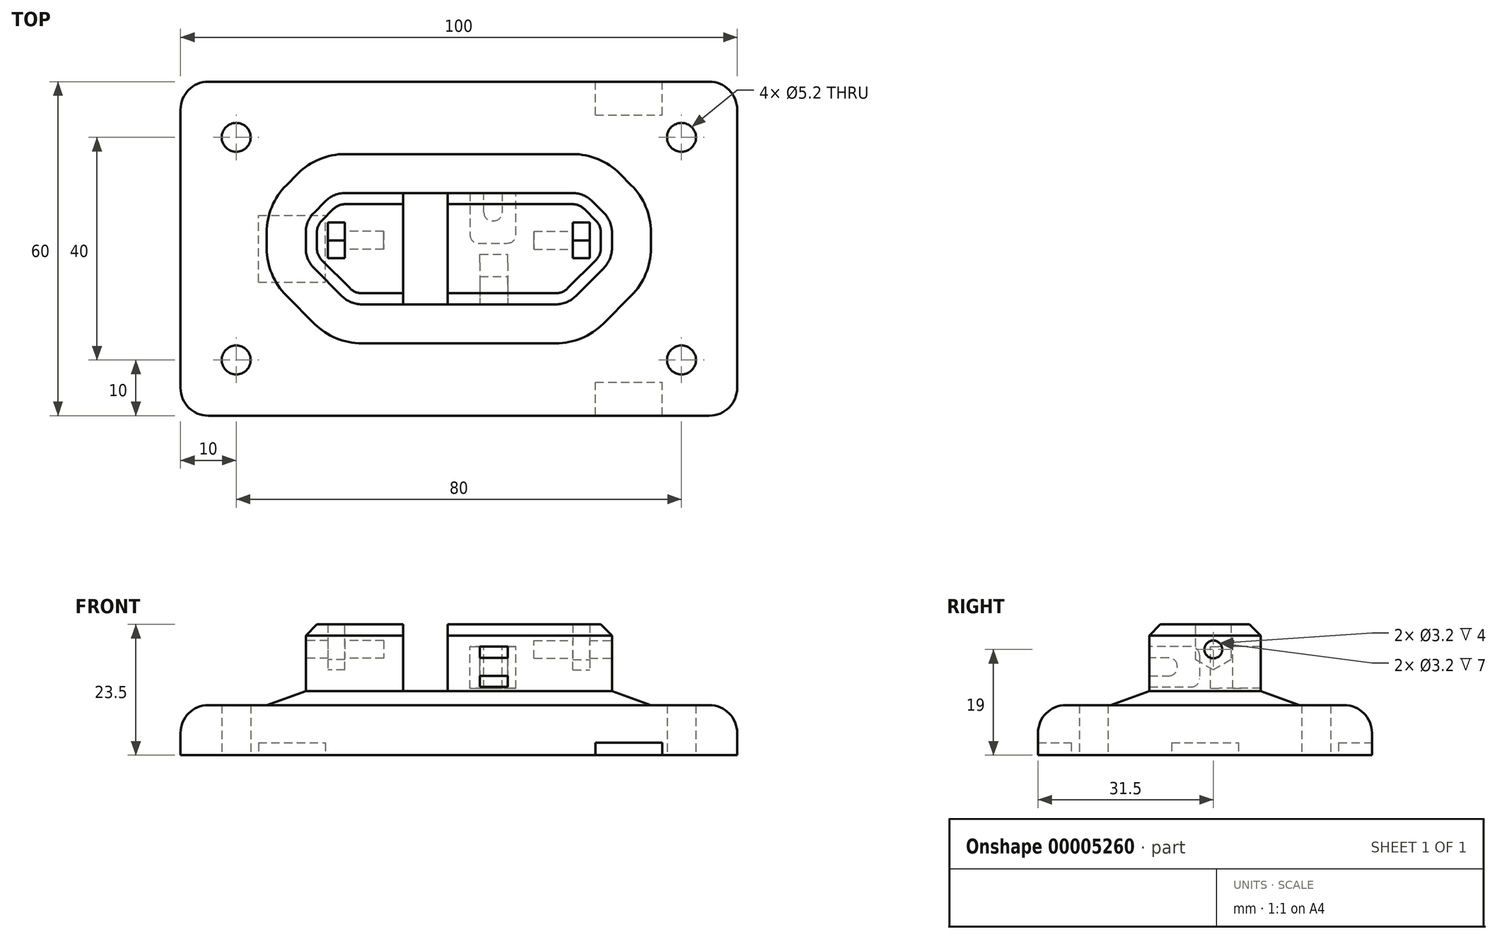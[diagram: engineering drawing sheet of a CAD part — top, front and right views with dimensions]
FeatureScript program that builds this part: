
annotation { "Feature Type Name" : "Feature", "Feature Type Description" : "" }
export const myFeature = defineFeature(function(context is Context, id is Id, definition is map)
    precondition{}
    {
        {
            var Q0;
            Q0=qCreatedBy(makeId("Top.planeOp"),FACE);
            var sketch = newSketch(context, id + "F0", { "sketchPlane" : qUnion([Q0])});
            skLineSegment(sketch, "E0.rect.bottom", {"start": v(-45, 30) * mm, "end": v(45, 30) * mm});
            skLineSegment(sketch, "E0.rect.top", {"start": v(-45, -30) * mm, "end": v(45, -30) * mm});
            skLineSegment(sketch, "E0.rect.left", {"start": v(-50, 25) * mm, "end": v(-50, -25) * mm});
            skLineSegment(sketch, "E0.rect.right", {"start": v(50, 25) * mm, "end": v(50, -25) * mm});
            skPoint(sketch, "E0.rect.middle", {"position": v(0, 0) * mm});
            skCircle(sketch, "E1", {"center": v(-40, 20) * mm, "radius": 2.6 * mm});
            skCircle(sketch, "E2", {"center": v(40, 20) * mm, "radius": 2.6 * mm});
            skCircle(sketch, "E3", {"center": v(40, -20) * mm, "radius": 2.6 * mm});
            skCircle(sketch, "E4", {"center": v(-40, -20) * mm, "radius": 2.6 * mm});
            skPoint(sketch, "E5.visualSharp", {"position": v(-50, 30) * mm});
            skArc(sketch, "E5.filletArc", {"start": v(-45, 30) * mm, "mid": v(-48.54, 28.54) * mm, "end": v(-50, 25) * mm});
            skPoint(sketch, "E6.visualSharp", {"position": v(50, 30) * mm});
            skArc(sketch, "E6.filletArc", {"start": v(50, 25) * mm, "mid": v(48.54, 28.54) * mm, "end": v(45, 30) * mm});
            skPoint(sketch, "E7.visualSharp", {"position": v(50, -30) * mm});
            skArc(sketch, "E7.filletArc", {"start": v(45, -30) * mm, "mid": v(48.54, -28.54) * mm, "end": v(50, -25) * mm});
            skPoint(sketch, "E8.visualSharp", {"position": v(-50, -30) * mm});
            skArc(sketch, "E8.filletArc", {"start": v(-50, -25) * mm, "mid": v(-48.54, -28.54) * mm, "end": v(-45, -30) * mm});
            skSolve(sketch);
        }
        {
            var Q0;
            Q0=qSketchRegion(id+"F0",true);
            extrude(context, id + "F1", {"entities" : qUnion([Q0]), "depth" : 9 * mm});
        }
        {
            var Q0;
            Q0=makeQuery(id+"F1.opExtrude","CAP_FACE",FACE,{"disambiguationData":[OSD([sQuery(id+"F0.wireOp",EDGE,"E0.rect.bottom"),sQuery(id+"F0.wireOp",EDGE,"E0.rect.top"),sQuery(id+"F0.wireOp",EDGE,"E0.rect.left"),sQuery(id+"F0.wireOp",EDGE,"E0.rect.right"),sQuery(id+"F0.wireOp",EDGE,"E1"),sQuery(id+"F0.wireOp",EDGE,"E2"),sQuery(id+"F0.wireOp",EDGE,"E3"),sQuery(id+"F0.wireOp",EDGE,"E4"),sQuery(id+"F0.wireOp",EDGE,"E5.filletArc"),sQuery(id+"F0.wireOp",EDGE,"E6.filletArc"),sQuery(id+"F0.wireOp",EDGE,"E7.filletArc"),sQuery(id+"F0.wireOp",EDGE,"E8.filletArc")])],"isStart":true});
            var sketch = newSketch(context, id + "F2", { "sketchPlane" : qUnion([Q0])});
            skLineSegment(sketch, "E9.rect.bottom", {"start": v(-36, 6) * mm, "end": v(-24, 6) * mm});
            skLineSegment(sketch, "E9.rect.top", {"start": v(-36, -6) * mm, "end": v(-24, -6) * mm});
            skLineSegment(sketch, "E9.rect.left", {"start": v(-36, 6) * mm, "end": v(-36, -6) * mm});
            skLineSegment(sketch, "E9.rect.right", {"start": v(-24, 6) * mm, "end": v(-24, -6) * mm});
            skPoint(sketch, "E9.rect.middle", {"position": v(-30, 0) * mm});
            skLineSegment(sketch, "E10.rect.bottom", {"start": v(24.52, 36) * mm, "end": v(36.52, 36) * mm});
            skLineSegment(sketch, "E10.rect.top", {"start": v(24.52, 24) * mm, "end": v(36.52, 24) * mm});
            skLineSegment(sketch, "E10.rect.left", {"start": v(24.52, 36) * mm, "end": v(24.52, 24) * mm});
            skLineSegment(sketch, "E10.rect.right", {"start": v(36.52, 36) * mm, "end": v(36.52, 24) * mm});
            skPoint(sketch, "E10.rect.middle", {"position": v(30.52, 30) * mm});
            skLineSegment(sketch, "E11.rect.bottom", {"start": v(24.52, -24) * mm, "end": v(36.52, -24) * mm});
            skLineSegment(sketch, "E11.rect.top", {"start": v(24.52, -36) * mm, "end": v(36.52, -36) * mm});
            skLineSegment(sketch, "E11.rect.left", {"start": v(24.52, -24) * mm, "end": v(24.52, -36) * mm});
            skLineSegment(sketch, "E11.rect.right", {"start": v(36.52, -24) * mm, "end": v(36.52, -36) * mm});
            skPoint(sketch, "E11.rect.middle", {"position": v(30.52, -30) * mm});
            skLineSegment(sketch, "E12", {"start": v(0, 0) * mm, "end": v(50, 0) * mm});
            skSolve(sketch);
        }
        {
            var Q0;
            Q0=qSketchRegion(id+"F2",true);
            extrude(context, id + "F3", {"entities" : qUnion([Q0]), "operationType" : NewBodyOperationType.REMOVE, "oppositeDirection" : true, "depth" : 2.25 * mm});
        }
        {
            var Q0;
            Q0=makeQuery(id+"F1.opExtrude","CAP_FACE",FACE,{"disambiguationData":[OSD([sQuery(id+"F0.wireOp",EDGE,"E0.rect.bottom"),sQuery(id+"F0.wireOp",EDGE,"E0.rect.top"),sQuery(id+"F0.wireOp",EDGE,"E0.rect.left"),sQuery(id+"F0.wireOp",EDGE,"E0.rect.right"),sQuery(id+"F0.wireOp",EDGE,"E1"),sQuery(id+"F0.wireOp",EDGE,"E2"),sQuery(id+"F0.wireOp",EDGE,"E3"),sQuery(id+"F0.wireOp",EDGE,"E4"),sQuery(id+"F0.wireOp",EDGE,"E5.filletArc"),sQuery(id+"F0.wireOp",EDGE,"E6.filletArc"),sQuery(id+"F0.wireOp",EDGE,"E7.filletArc"),sQuery(id+"F0.wireOp",EDGE,"E8.filletArc")])],"isStart":false});
            var sketch = newSketch(context, id + "F4", { "sketchPlane" : qUnion([Q0])});
            skPoint(sketch, "E13.orphan", {"position": v(-50, 0) * mm});
            skPoint(sketch, "E14.end.orphan", {"position": v(50, 0) * mm});
            skLineSegment(sketch, "E15.rect.bottom", {"start": v(-27.5, 10) * mm, "end": v(27.5, 10) * mm});
            skLineSegment(sketch, "E15.rect.top", {"start": v(-27.5, -10) * mm, "end": v(27.5, -10) * mm});
            skLineSegment(sketch, "E15.rect.left", {"start": v(-27.5, 10) * mm, "end": v(-27.5, -10) * mm});
            skLineSegment(sketch, "E15.rect.right", {"start": v(27.5, 10) * mm, "end": v(27.5, -10) * mm});
            skPoint(sketch, "E15.rect.middle", {"position": v(0, 0) * mm});
            skSolve(sketch);
        }
        {
            var Q0;
            Q0=qSketchRegion(id+"F4",true);
            extrude(context, id + "F5", {"entities" : qUnion([Q0]), "operationType" : NewBodyOperationType.ADD, "depth" : 14.5 * mm});
        }
        {
            var Q0;
            Q0=makeQuery(id+"F5.opExtrude","SWEPT_EDGE",EDGE,{"disambiguationData":[OSD([sQuery(id+"F4.wireOp",EDGE,"E15.rect.top"),sQuery(id+"F4.wireOp",EDGE,"E15.rect.left")])]});
            var Q1;
            Q1=makeQuery(id+"F5.opExtrude","SWEPT_EDGE",EDGE,{"disambiguationData":[OSD([sQuery(id+"F4.wireOp",EDGE,"E15.rect.top"),sQuery(id+"F4.wireOp",EDGE,"E15.rect.right")])]});
            chamfer(context, id + "F6", {"entities" : qUnion([Q0, Q1]), "width" : 8 * mm, "tangentPropagation" : true});
        }
        {
            var Q0;
            Q0=makeQuery(id+"F5.opExtrude","SWEPT_EDGE",EDGE,{"disambiguationData":[OSD([sQuery(id+"F4.wireOp",EDGE,"E15.rect.bottom"),sQuery(id+"F4.wireOp",EDGE,"E15.rect.left")])]});
            var Q1;
            Q1=makeQuery(id+"F5.opExtrude","SWEPT_EDGE",EDGE,{"disambiguationData":[OSD([sQuery(id+"F4.wireOp",EDGE,"E15.rect.bottom"),sQuery(id+"F4.wireOp",EDGE,"E15.rect.right")])]});
            chamfer(context, id + "F7", {"entities" : qUnion([Q0, Q1]), "width" : 5 * mm, "tangentPropagation" : true});
        }
        {
            var Q0;
            Q0=makeQuery(id+"F5.opExtrude","CAP_FACE",FACE,{"disambiguationData":[OSD([sQuery(id+"F4.wireOp",EDGE,"E15.rect.bottom"),sQuery(id+"F4.wireOp",EDGE,"E15.rect.top"),sQuery(id+"F4.wireOp",EDGE,"E15.rect.left"),sQuery(id+"F4.wireOp",EDGE,"E15.rect.right")])],"isStart":false});
            var sketch = newSketch(context, id + "F8", { "sketchPlane" : qUnion([Q0])});
            skLineSegment(sketch, "E16.rect.bottom", {"start": v(-10, 10) * mm, "end": v(-2, 10) * mm});
            skLineSegment(sketch, "E16.rect.top", {"start": v(-10, -10) * mm, "end": v(-2, -10) * mm});
            skLineSegment(sketch, "E16.rect.left", {"start": v(-10, 10) * mm, "end": v(-10, -10) * mm});
            skLineSegment(sketch, "E16.rect.right", {"start": v(-2, 10) * mm, "end": v(-2, -10) * mm});
            skPoint(sketch, "E16.rect.middle", {"position": v(-6, 0) * mm});
            skSolve(sketch);
        }
        {
            var Q0;
            Q0=qSketchRegion(id+"F8",true);
            extrude(context, id + "F9", {"entities" : qUnion([Q0]), "operationType" : NewBodyOperationType.REMOVE, "oppositeDirection" : true, "depth" : 12 * mm});
        }
        {
            var Q0;
            {var subQ0=sQuery(id+"F4.wireOp",EDGE,"E15.rect.bottom");var subQ1=sQuery(id+"F4.wireOp",EDGE,"E15.rect.top");var subQ2=sQuery(id+"F4.wireOp",EDGE,"E15.rect.right");Q0=makeQuery(id+"F9.boolean.opBoolean","SPLIT",FACE,{"disambiguationData":[TD([makeQuery(id+"F5.opExtrude","SWEPT_FACE",FACE,{"disambiguationData":[OSD([subQ2])]})])],"derivedFrom":makeQuery(id+"F5.opExtrude","CAP_FACE",FACE,{"disambiguationData":[OSD([subQ0,subQ1,sQuery(id+"F4.wireOp",EDGE,"E15.rect.left"),subQ2])],"isStart":false})});}
            cPlane(context, id + "F10", {"entities" : qUnion([Q0]), "cplaneType" : CPlaneType.OFFSET, "offset" : 4 * mm, "oppositeDirection" : true, "width" : 150 * mm, "height" : 150 * mm});
        }
        {
            var Q0;
            Q0=makeQuery(id+"F5.opExtrude","SWEPT_FACE",FACE,{"disambiguationData":[OSD([sQuery(id+"F4.wireOp",EDGE,"E15.rect.left")])]});
            var sketch = newSketch(context, id + "F11", { "sketchPlane" : qUnion([Q0])});
            skCircle(sketch, "E17", {"center": v(-1.5, 19) * mm, "radius": 1.6 * mm});
            skSolve(sketch);
        }
        {
            var Q0;
            Q0=qSketchRegion(id+"F11",true);
            extrude(context, id + "F12", {"entities" : qUnion([Q0]), "operationType" : NewBodyOperationType.REMOVE, "oppositeDirection" : true, "depth" : 14 * mm});
        }
        {
            var Q0;
            Q0=makeQuery(id+"F5.opExtrude","SWEPT_FACE",FACE,{"disambiguationData":[OSD([sQuery(id+"F4.wireOp",EDGE,"E15.rect.right")])]});
            var sketch = newSketch(context, id + "F13", { "sketchPlane" : qUnion([Q0])});
            skCircle(sketch, "E18", {"center": v(1.5, 19) * mm, "radius": 1.6 * mm});
            skSolve(sketch);
        }
        {
            var Q0;
            Q0=qSketchRegion(id+"F13",true);
            extrude(context, id + "F14", {"entities" : qUnion([Q0]), "operationType" : NewBodyOperationType.REMOVE, "oppositeDirection" : true, "depth" : 14 * mm});
        }
        {
            var Q0;
            Q0=qCreatedBy(id+"F10.planeOp",FACE);
            var sketch = newSketch(context, id + "F15", { "sketchPlane" : qUnion([Q0])});
            skLineSegment(sketch, "E19", {"start": v(2, 10) * mm, "end": v(2, 1) * mm});
            skLineSegment(sketch, "E20", {"start": v(2, 1) * mm, "end": v(10.25, 1) * mm});
            skLineSegment(sketch, "E21", {"start": v(10.25, 1) * mm, "end": v(10.25, 10) * mm});
            skLineSegment(sketch, "E22", {"start": v(10.25, 10) * mm, "end": v(7.75, 10) * mm});
            skLineSegment(sketch, "E23", {"start": v(7.75, 10) * mm, "end": v(7.75, 5) * mm});
            skLineSegment(sketch, "E24", {"start": v(7.75, 5) * mm, "end": v(4.5, 5) * mm});
            skLineSegment(sketch, "E25", {"start": v(4.5, 5) * mm, "end": v(4.5, 10) * mm});
            skLineSegment(sketch, "E26", {"start": v(4.5, 10) * mm, "end": v(2, 10) * mm});
            skSolve(sketch);
        }
        {
            var Q0;
            Q0=qSketchRegion(id+"F15",true);
            extrude(context, id + "F16", {"entities" : qUnion([Q0]), "operationType" : NewBodyOperationType.REMOVE, "oppositeDirection" : true, "depth" : 7.5 * mm});
        }
        {
            var Q0;
            Q0=qCreatedBy(makeId("Right.planeOp"),FACE);
            cPlane(context, id + "F17", {"entities" : qUnion([Q0]), "cplaneType" : CPlaneType.OFFSET, "offset" : 8.8 * mm, "width" : 150 * mm, "height" : 150 * mm});
        }
        {
            var Q0;
            Q0=qCreatedBy(id+"F17.planeOp",FACE);
            var sketch = newSketch(context, id + "F18", { "sketchPlane" : qUnion([Q0])});
            skLineSegment(sketch, "E27", {"start": v(-10, 12.25) * mm, "end": v(-1, 12.25) * mm});
            skLineSegment(sketch, "E28", {"start": v(-1, 19.5) * mm, "end": v(-10, 19.5) * mm});
            skLineSegment(sketch, "E29", {"start": v(-10, 19.5) * mm, "end": v(-10, 17.5) * mm});
            skLineSegment(sketch, "E30", {"start": v(-1, 19.5) * mm, "end": v(-1, 12.25) * mm});
            skLineSegment(sketch, "E31", {"start": v(-10, 14.25) * mm, "end": v(-5, 14.25) * mm});
            skLineSegment(sketch, "E32", {"start": v(-5, 14.25) * mm, "end": v(-5, 17.5) * mm});
            skLineSegment(sketch, "E33", {"start": v(-5, 17.5) * mm, "end": v(-10, 17.5) * mm});
            skLineSegment(sketch, "E34.trimOffspring", {"start": v(-10, 14.25) * mm, "end": v(-10, 12.25) * mm});
            skSolve(sketch);
        }
        {
            var Q0;
            Q0=qSketchRegion(id+"F18",true);
            extrude(context, id + "F19", {"entities" : qUnion([Q0]), "operationType" : NewBodyOperationType.REMOVE, "oppositeDirection" : true, "depth" : 5 * mm});
        }
        {
            var Q0;
            Q0=makeQuery(id+"F16.boolean.opBoolean","COPY",EDGE,{"derivedFrom":makeQuery(id+"F16.opExtrude","SWEPT_EDGE",EDGE,{"disambiguationData":[OSD([sQuery(id+"F15.wireOp",EDGE,"b27fa09f-654b-4976-832a-8cd4d72e1bcd"),sQuery(id+"F15.wireOp",EDGE,"0d0e19da-8f42-4381-b15f-3c7ce20022dd")])]})});
            var Q1;
            Q1=makeQuery(id+"F16.boolean.opBoolean","COPY",EDGE,{"derivedFrom":makeQuery(id+"F16.opExtrude","SWEPT_EDGE",EDGE,{"disambiguationData":[OSD([sQuery(id+"F15.wireOp",EDGE,"0d0e19da-8f42-4381-b15f-3c7ce20022dd"),sQuery(id+"F15.wireOp",EDGE,"007b9c6f-361a-4d94-a8b3-a32368527ee9")])]})});
            var Q2;
            Q2=makeQuery(id+"F16.boolean.opBoolean","COPY",EDGE,{"derivedFrom":makeQuery(id+"F16.opExtrude","SWEPT_EDGE",EDGE,{"disambiguationData":[OSD([sQuery(id+"F15.wireOp",EDGE,"966db383-c47d-4d1a-9eee-fc0741a5b44d"),sQuery(id+"F15.wireOp",EDGE,"9a90bedf-13ad-46d5-b3b2-74371d44ae28")])]})});
            var Q3;
            Q3=makeQuery(id+"F16.boolean.opBoolean","COPY",EDGE,{"derivedFrom":makeQuery(id+"F16.opExtrude","SWEPT_EDGE",EDGE,{"disambiguationData":[OSD([sQuery(id+"F15.wireOp",EDGE,"9a90bedf-13ad-46d5-b3b2-74371d44ae28"),sQuery(id+"F15.wireOp",EDGE,"3751e907-f0bc-4d0a-a093-d6da3d786c70")])]})});
            var Q4;
            Q4=makeQuery(id+"F16.boolean.opBoolean","COPY",EDGE,{"derivedFrom":makeQuery(id+"F16.opExtrude","SWEPT_EDGE",EDGE,{"disambiguationData":[OSD([sQuery(id+"F15.wireOp",EDGE,"E24"),sQuery(id+"F15.wireOp",EDGE,"E25")])]})});
            var Q5;
            Q5=makeQuery(id+"F16.boolean.opBoolean","COPY",EDGE,{"derivedFrom":makeQuery(id+"F16.opExtrude","SWEPT_EDGE",EDGE,{"disambiguationData":[OSD([sQuery(id+"F15.wireOp",EDGE,"E23"),sQuery(id+"F15.wireOp",EDGE,"E24")])]})});
            var Q6;
            Q6=makeQuery(id+"F16.boolean.opBoolean","COPY",EDGE,{"derivedFrom":makeQuery(id+"F16.opExtrude","SWEPT_EDGE",EDGE,{"disambiguationData":[OSD([sQuery(id+"F15.wireOp",EDGE,"E19"),sQuery(id+"F15.wireOp",EDGE,"E20")])]})});
            var Q7;
            Q7=makeQuery(id+"F16.boolean.opBoolean","COPY",EDGE,{"derivedFrom":makeQuery(id+"F16.opExtrude","SWEPT_EDGE",EDGE,{"disambiguationData":[OSD([sQuery(id+"F15.wireOp",EDGE,"E20"),sQuery(id+"F15.wireOp",EDGE,"E21")])]})});
            var Q8;
            Q8=makeQuery(id+"F19.boolean.opBoolean","COPY",EDGE,{"derivedFrom":makeQuery(id+"F19.opExtrude","SWEPT_EDGE",EDGE,{"disambiguationData":[OSD([sQuery(id+"F18.wireOp",EDGE,"E32"),sQuery(id+"F18.wireOp",EDGE,"E33")])]})});
            var Q9;
            Q9=makeQuery(id+"F19.boolean.opBoolean","COPY",EDGE,{"derivedFrom":makeQuery(id+"F19.opExtrude","SWEPT_EDGE",EDGE,{"disambiguationData":[OSD([sQuery(id+"F18.wireOp",EDGE,"E31"),sQuery(id+"F18.wireOp",EDGE,"E32")])]})});
            var Q10;
            Q10=makeQuery(id+"F19.boolean.opBoolean","COPY",EDGE,{"derivedFrom":makeQuery(id+"F19.opExtrude","SWEPT_EDGE",EDGE,{"disambiguationData":[OSD([sQuery(id+"F18.wireOp",EDGE,"E28"),sQuery(id+"F18.wireOp",EDGE,"E30")])]})});
            var Q11;
            Q11=makeQuery(id+"F19.boolean.opBoolean","COPY",EDGE,{"derivedFrom":makeQuery(id+"F19.opExtrude","SWEPT_EDGE",EDGE,{"disambiguationData":[OSD([sQuery(id+"F18.wireOp",EDGE,"E27"),sQuery(id+"F18.wireOp",EDGE,"E30")])]})});
            fillet(context, id + "F20", {"entities" : qUnion([Q0, Q1, Q2, Q3, Q4, Q5, Q6, Q7, Q8, Q9, Q10, Q11]), "radius" : 1.5 * mm, "tangentPropagation" : true, "allowEdgeOverflow" : false});
        }
        {
            var Q0;
            Q0=makeQuery(id+"F5.opExtrude","SWEPT_FACE",FACE,{"disambiguationData":[OSD([sQuery(id+"F4.wireOp",EDGE,"E15.rect.right")])]});
            cPlane(context, id + "F21", {"entities" : qUnion([Q0]), "cplaneType" : CPlaneType.OFFSET, "offset" : 4 * mm, "oppositeDirection" : true, "width" : 150 * mm, "height" : 150 * mm});
        }
        {
            var Q0;
            Q0=qCreatedBy(id+"F21.planeOp",FACE);
            var sketch = newSketch(context, id + "F22", { "sketchPlane" : qUnion([Q0])});
            skCircle(sketch, "E35.cCircle", {"center": v(1.5, 19) * mm, "radius": 3.2 * mm, "construction": true});
            skLineSegment(sketch, "E35.0", {"start": v(-1.7, 17.15) * mm, "end": v(-1.7, 20.85) * mm});
            skLineSegment(sketch, "E35.1", {"start": v(-1.7, 20.85) * mm, "end": v(1.5, 22.7) * mm});
            skLineSegment(sketch, "E35.2", {"start": v(1.5, 22.7) * mm, "end": v(4.7, 20.85) * mm});
            skLineSegment(sketch, "E35.3", {"start": v(4.7, 20.85) * mm, "end": v(4.7, 17.15) * mm});
            skLineSegment(sketch, "E35.4", {"start": v(4.7, 17.15) * mm, "end": v(1.5, 15.3) * mm});
            skLineSegment(sketch, "E35.5", {"start": v(1.5, 15.3) * mm, "end": v(-1.7, 17.15) * mm});
            skPoint(sketch, "E35.0.midPoint", {"position": v(-1.7, 19) * mm});
            skLineSegment(sketch, "E36", {"start": v(-1.7, 20.85) * mm, "end": v(-1.7, 23.5) * mm});
            skLineSegment(sketch, "E37", {"start": v(-1.7, 23.5) * mm, "end": v(4.7, 23.5) * mm});
            skLineSegment(sketch, "E38", {"start": v(4.7, 23.5) * mm, "end": v(4.7, 20.85) * mm});
            skSolve(sketch);
        }
        {
            var Q0;
            Q0=qSketchRegion(id+"F22",true);
            extrude(context, id + "F23", {"entities" : qUnion([Q0]), "operationType" : NewBodyOperationType.REMOVE, "oppositeDirection" : true, "depth" : 3 * mm});
        }
        {
            var Q0;
            Q0=makeQuery(id+"F5.opExtrude","SWEPT_FACE",FACE,{"disambiguationData":[OSD([sQuery(id+"F4.wireOp",EDGE,"E15.rect.left")])]});
            cPlane(context, id + "F24", {"entities" : qUnion([Q0]), "cplaneType" : CPlaneType.OFFSET, "offset" : 4 * mm, "oppositeDirection" : true, "width" : 150 * mm, "height" : 150 * mm});
        }
        {
            var Q0;
            Q0=qCreatedBy(id+"F24.planeOp",FACE);
            var sketch = newSketch(context, id + "F25", { "sketchPlane" : qUnion([Q0])});
            skCircle(sketch, "E39.cCircle", {"center": v(-1.5, 19) * mm, "radius": 3.2 * mm, "construction": true});
            skLineSegment(sketch, "E39.0", {"start": v(-4.7, 20.85) * mm, "end": v(-1.5, 22.7) * mm});
            skLineSegment(sketch, "E39.1", {"start": v(-1.5, 22.7) * mm, "end": v(1.7, 20.85) * mm});
            skLineSegment(sketch, "E39.2", {"start": v(1.7, 20.85) * mm, "end": v(1.7, 17.15) * mm});
            skLineSegment(sketch, "E39.3", {"start": v(1.7, 17.15) * mm, "end": v(-1.5, 15.3) * mm});
            skLineSegment(sketch, "E39.4", {"start": v(-1.5, 15.3) * mm, "end": v(-4.7, 17.15) * mm});
            skLineSegment(sketch, "E39.5", {"start": v(-4.7, 17.15) * mm, "end": v(-4.7, 20.85) * mm});
            skPoint(sketch, "E39.0.midPoint", {"position": v(-3.1, 21.77) * mm});
            skLineSegment(sketch, "E40", {"start": v(-4.7, 20.85) * mm, "end": v(-4.7, 23.5) * mm});
            skLineSegment(sketch, "E41", {"start": v(-4.7, 23.5) * mm, "end": v(1.7, 23.5) * mm});
            skLineSegment(sketch, "E42", {"start": v(1.7, 23.5) * mm, "end": v(1.7, 20.85) * mm});
            skSolve(sketch);
        }
        {
            var Q0;
            Q0=qSketchRegion(id+"F25",true);
            extrude(context, id + "F26", {"entities" : qUnion([Q0]), "operationType" : NewBodyOperationType.REMOVE, "oppositeDirection" : true, "depth" : 3 * mm});
        }
        {
            var Q0;
            Q0=makeQuery(id+"F1.opExtrude","CAP_EDGE",EDGE,{"disambiguationData":[OSD([sQuery(id+"F0.wireOp",EDGE,"E0.rect.top")])],"isStart":false});
            fillet(context, id + "F27", {"entities" : qUnion([Q0]), "radius" : 5 * mm, "tangentPropagation" : true, "allowEdgeOverflow" : false});
        }
        {
            var Q0;
            {var subQ0=sQuery(id+"F4.wireOp",EDGE,"E15.rect.top");Q0=makeQuery(id+"F6.opChamfer","BLEND_EDGE",EDGE,{"blendedFrom":[makeQuery(id+"F5.opExtrude","SWEPT_EDGE",EDGE,{"disambiguationData":[OSD([subQ0,sQuery(id+"F4.wireOp",EDGE,"E15.rect.left")])]}),makeQuery(id+"F5.opExtrude","SWEPT_FACE",FACE,{"disambiguationData":[OSD([subQ0])]})],"blendedInto":[makeQuery(id+"F5.opExtrude","SWEPT_FACE",FACE,{"disambiguationData":[OSD([subQ0])]})]});}
            var Q1;
            {var subQ0=sQuery(id+"F4.wireOp",EDGE,"E15.rect.left");Q1=makeQuery(id+"F6.opChamfer","BLEND_EDGE",EDGE,{"blendedFrom":[makeQuery(id+"F5.opExtrude","SWEPT_EDGE",EDGE,{"disambiguationData":[OSD([sQuery(id+"F4.wireOp",EDGE,"E15.rect.top"),subQ0])]}),makeQuery(id+"F5.opExtrude","SWEPT_FACE",FACE,{"disambiguationData":[OSD([subQ0])]})],"blendedInto":[makeQuery(id+"F5.opExtrude","SWEPT_FACE",FACE,{"disambiguationData":[OSD([subQ0])]})]});}
            var Q2;
            {var subQ0=sQuery(id+"F4.wireOp",EDGE,"E15.rect.left");Q2=makeQuery(id+"F7.opChamfer","BLEND_EDGE",EDGE,{"blendedFrom":[makeQuery(id+"F5.opExtrude","SWEPT_EDGE",EDGE,{"disambiguationData":[OSD([sQuery(id+"F4.wireOp",EDGE,"E15.rect.bottom"),subQ0])]}),makeQuery(id+"F5.opExtrude","SWEPT_FACE",FACE,{"disambiguationData":[OSD([subQ0])]})],"blendedInto":[makeQuery(id+"F5.opExtrude","SWEPT_FACE",FACE,{"disambiguationData":[OSD([subQ0])]})]});}
            var Q3;
            {var subQ0=sQuery(id+"F4.wireOp",EDGE,"E15.rect.bottom");Q3=makeQuery(id+"F7.opChamfer","BLEND_EDGE",EDGE,{"blendedFrom":[makeQuery(id+"F5.opExtrude","SWEPT_EDGE",EDGE,{"disambiguationData":[OSD([subQ0,sQuery(id+"F4.wireOp",EDGE,"E15.rect.left")])]}),makeQuery(id+"F5.opExtrude","SWEPT_FACE",FACE,{"disambiguationData":[OSD([subQ0])]})],"blendedInto":[makeQuery(id+"F5.opExtrude","SWEPT_FACE",FACE,{"disambiguationData":[OSD([subQ0])]})]});}
            var Q4;
            Q4=makeQuery(id+"F9.boolean.opBoolean","COPY",EDGE,{"derivedFrom":makeQuery(id+"F9.opExtrude","SWEPT_EDGE",EDGE,{"disambiguationData":[OSD([sQuery(id+"F4.wireOp",EDGE,"E15.rect.top"),sQuery(id+"F8.wireOp",EDGE,"E16.rect.top"),sQuery(id+"F8.wireOp",EDGE,"E16.rect.left")])]})});
            var Q5;
            Q5=makeQuery(id+"F9.boolean.opBoolean","COPY",EDGE,{"derivedFrom":makeQuery(id+"F9.opExtrude","SWEPT_EDGE",EDGE,{"disambiguationData":[OSD([sQuery(id+"F4.wireOp",EDGE,"E15.rect.bottom"),sQuery(id+"F8.wireOp",EDGE,"E16.rect.bottom"),sQuery(id+"F8.wireOp",EDGE,"E16.rect.left")])]})});
            var Q6;
            Q6=makeQuery(id+"F9.boolean.opBoolean","COPY",EDGE,{"derivedFrom":makeQuery(id+"F9.opExtrude","SWEPT_EDGE",EDGE,{"disambiguationData":[OSD([sQuery(id+"F4.wireOp",EDGE,"E15.rect.bottom"),sQuery(id+"F8.wireOp",EDGE,"E16.rect.bottom"),sQuery(id+"F8.wireOp",EDGE,"E16.rect.right")])]})});
            var Q7;
            Q7=makeQuery(id+"F9.boolean.opBoolean","COPY",EDGE,{"derivedFrom":makeQuery(id+"F9.opExtrude","SWEPT_EDGE",EDGE,{"disambiguationData":[OSD([sQuery(id+"F4.wireOp",EDGE,"E15.rect.top"),sQuery(id+"F8.wireOp",EDGE,"E16.rect.top"),sQuery(id+"F8.wireOp",EDGE,"E16.rect.right")])]})});
            var Q8;
            {var subQ0=sQuery(id+"F4.wireOp",EDGE,"E15.rect.top");Q8=makeQuery(id+"F6.opChamfer","BLEND_EDGE",EDGE,{"blendedFrom":[makeQuery(id+"F5.opExtrude","SWEPT_EDGE",EDGE,{"disambiguationData":[OSD([subQ0,sQuery(id+"F4.wireOp",EDGE,"E15.rect.right")])]}),makeQuery(id+"F5.opExtrude","SWEPT_FACE",FACE,{"disambiguationData":[OSD([subQ0])]})],"blendedInto":[makeQuery(id+"F5.opExtrude","SWEPT_FACE",FACE,{"disambiguationData":[OSD([subQ0])]})]});}
            var Q9;
            {var subQ0=sQuery(id+"F4.wireOp",EDGE,"E15.rect.right");Q9=makeQuery(id+"F6.opChamfer","BLEND_EDGE",EDGE,{"blendedFrom":[makeQuery(id+"F5.opExtrude","SWEPT_EDGE",EDGE,{"disambiguationData":[OSD([sQuery(id+"F4.wireOp",EDGE,"E15.rect.top"),subQ0])]}),makeQuery(id+"F5.opExtrude","SWEPT_FACE",FACE,{"disambiguationData":[OSD([subQ0])]})],"blendedInto":[makeQuery(id+"F5.opExtrude","SWEPT_FACE",FACE,{"disambiguationData":[OSD([subQ0])]})]});}
            var Q10;
            {var subQ0=sQuery(id+"F4.wireOp",EDGE,"E15.rect.right");Q10=makeQuery(id+"F7.opChamfer","BLEND_EDGE",EDGE,{"blendedFrom":[makeQuery(id+"F5.opExtrude","SWEPT_EDGE",EDGE,{"disambiguationData":[OSD([sQuery(id+"F4.wireOp",EDGE,"E15.rect.bottom"),subQ0])]}),makeQuery(id+"F5.opExtrude","SWEPT_FACE",FACE,{"disambiguationData":[OSD([subQ0])]})],"blendedInto":[makeQuery(id+"F5.opExtrude","SWEPT_FACE",FACE,{"disambiguationData":[OSD([subQ0])]})]});}
            var Q11;
            {var subQ0=sQuery(id+"F4.wireOp",EDGE,"E15.rect.bottom");Q11=makeQuery(id+"F7.opChamfer","BLEND_EDGE",EDGE,{"blendedFrom":[makeQuery(id+"F5.opExtrude","SWEPT_EDGE",EDGE,{"disambiguationData":[OSD([subQ0,sQuery(id+"F4.wireOp",EDGE,"E15.rect.right")])]}),makeQuery(id+"F5.opExtrude","SWEPT_FACE",FACE,{"disambiguationData":[OSD([subQ0])]})],"blendedInto":[makeQuery(id+"F5.opExtrude","SWEPT_FACE",FACE,{"disambiguationData":[OSD([subQ0])]})]});}
            fillet(context, id + "F28", {"entities" : qUnion([Q0, Q1, Q2, Q3, Q4, Q5, Q6, Q7, Q8, Q9, Q10, Q11]), "radius" : 5 * mm, "tangentPropagation" : true, "allowEdgeOverflow" : false});
        }
        {
            var Q0;
            Q0=makeQuery(id+"F5.opExtrude","CAP_EDGE",EDGE,{"disambiguationData":[OSD([sQuery(id+"F4.wireOp",EDGE,"E15.rect.left")])],"isStart":false});
            var Q1;
            Q1=makeQuery(id+"F5.opExtrude","CAP_EDGE",EDGE,{"disambiguationData":[OSD([sQuery(id+"F4.wireOp",EDGE,"E15.rect.right")])],"isStart":false});
            chamfer(context, id + "F29", {"entities" : qUnion([Q0, Q1]), "width" : 2 * mm, "tangentPropagation" : true});
        }
        {
            var Q0;
            Q0=makeQuery(id+"F6.opChamfer","BLEND_EDGE",EDGE,{"blendedFrom":[makeQuery(id+"F5.opExtrude","SWEPT_EDGE",EDGE,{"disambiguationData":[OSD([sQuery(id+"F4.wireOp",EDGE,"E15.rect.top"),sQuery(id+"F4.wireOp",EDGE,"E15.rect.left")])]}),makeQuery(id+"F1.opExtrude","CAP_FACE",FACE,{"disambiguationData":[OSD([sQuery(id+"F0.wireOp",EDGE,"E0.rect.bottom"),sQuery(id+"F0.wireOp",EDGE,"E0.rect.top"),sQuery(id+"F0.wireOp",EDGE,"E0.rect.left"),sQuery(id+"F0.wireOp",EDGE,"E0.rect.right"),sQuery(id+"F0.wireOp",EDGE,"E1"),sQuery(id+"F0.wireOp",EDGE,"E2"),sQuery(id+"F0.wireOp",EDGE,"E3"),sQuery(id+"F0.wireOp",EDGE,"E4"),sQuery(id+"F0.wireOp",EDGE,"E5.filletArc"),sQuery(id+"F0.wireOp",EDGE,"E6.filletArc"),sQuery(id+"F0.wireOp",EDGE,"E7.filletArc"),sQuery(id+"F0.wireOp",EDGE,"E8.filletArc")])],"isStart":false})],"blendedInto":[makeQuery(id+"F1.opExtrude","CAP_FACE",FACE,{"disambiguationData":[OSD([sQuery(id+"F0.wireOp",EDGE,"E0.rect.bottom"),sQuery(id+"F0.wireOp",EDGE,"E0.rect.top"),sQuery(id+"F0.wireOp",EDGE,"E0.rect.left"),sQuery(id+"F0.wireOp",EDGE,"E0.rect.right"),sQuery(id+"F0.wireOp",EDGE,"E1"),sQuery(id+"F0.wireOp",EDGE,"E2"),sQuery(id+"F0.wireOp",EDGE,"E3"),sQuery(id+"F0.wireOp",EDGE,"E4"),sQuery(id+"F0.wireOp",EDGE,"E5.filletArc"),sQuery(id+"F0.wireOp",EDGE,"E6.filletArc"),sQuery(id+"F0.wireOp",EDGE,"E7.filletArc"),sQuery(id+"F0.wireOp",EDGE,"E8.filletArc")])],"isStart":false})]});
            chamfer(context, id + "F30", {"entities" : qUnion([Q0]), "chamferType" : ChamferType.TWO_OFFSETS, "width1" : 7 * mm, "oppositeDirection" : false, "width2" : 2.5 * mm, "tangentPropagation" : true});
        }
    });
